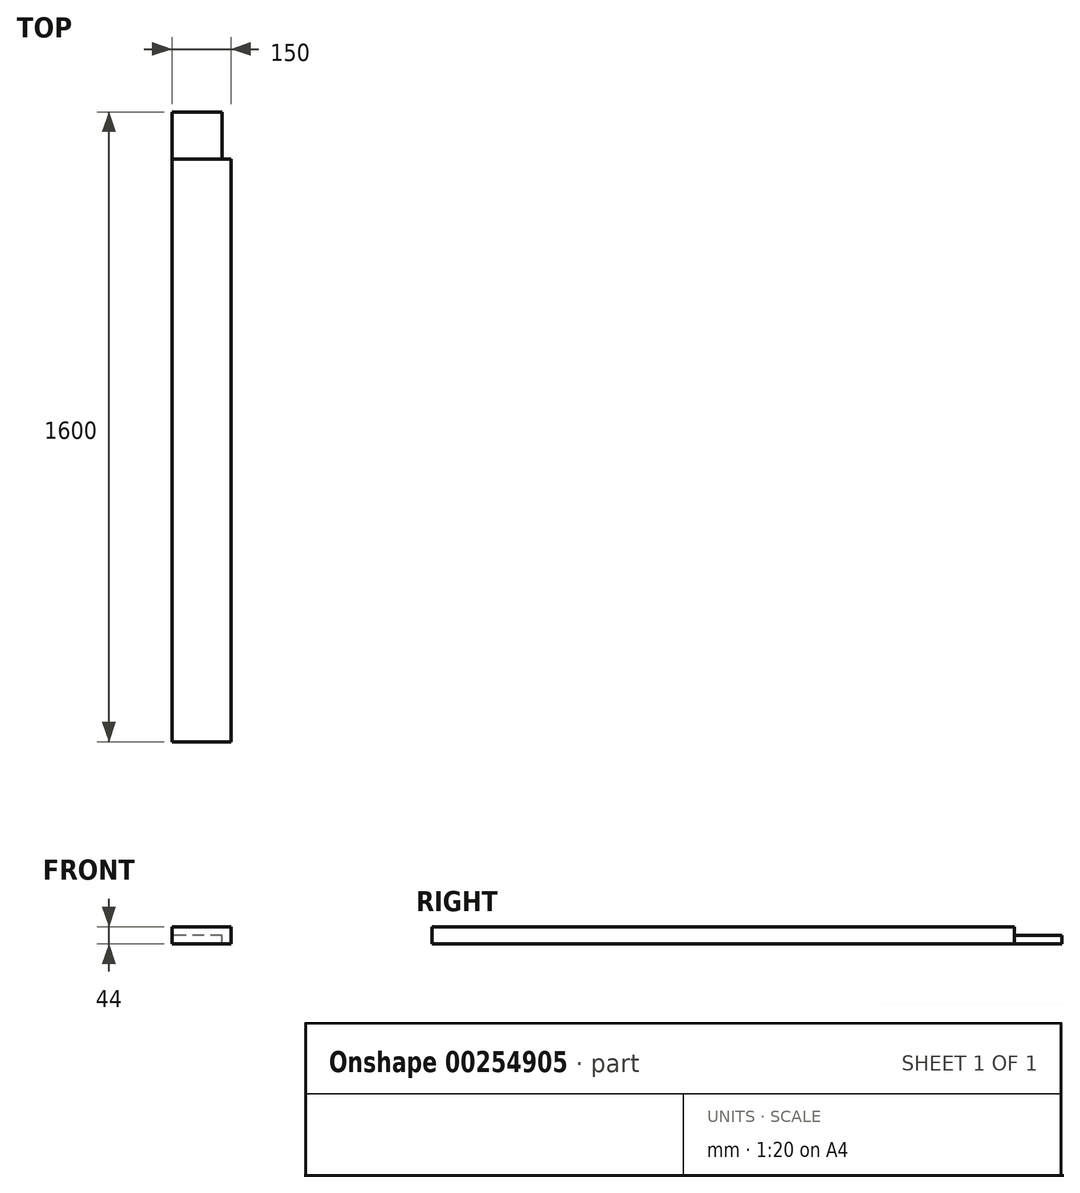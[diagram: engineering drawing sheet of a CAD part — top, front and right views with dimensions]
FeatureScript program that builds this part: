
annotation { "Feature Type Name" : "Feature", "Feature Type Description" : "" }
export const myFeature = defineFeature(function(context is Context, id is Id, definition is map)
    precondition{}
    {
        {
            var Q0;
            Q0=qCreatedBy(makeId("Front.planeOp"),FACE);
            var sketch = newSketch(context, id + "F0", { "sketchPlane" : qUnion([Q0])});
            skLineSegment(sketch, "E0.bottom", {"start": v(0, 0) * mm, "end": v(-150, 0) * mm});
            skLineSegment(sketch, "E0.top", {"start": v(0, 44) * mm, "end": v(-150, 44) * mm});
            skLineSegment(sketch, "E0.left", {"start": v(0, 0) * mm, "end": v(0, 44) * mm});
            skLineSegment(sketch, "E0.right", {"start": v(-150, 0) * mm, "end": v(-150, 44) * mm});
            skSolve(sketch);
        }
        {
            var Q0;
            Q0=makeQuery(id+"F0.imprint","IMPRINT",FACE,{"disambiguationData":[TD([[makeQuery(id+"F0.imprint","IMPRINT",EDGE,{"derivedFrom":sQuery(id+"F0.wireOp",EDGE,"E0.bottom")}),-1.0]])]});
            extrude(context, id + "F1", {"entities" : qUnion([Q0]), "oppositeDirection" : true, "depth" : 1600 * mm});
        }
        {
            var Q0;
            Q0=makeQuery(id+"F1.opExtrude","SWEPT_EDGE",EDGE,{"disambiguationData":[OSD([sQuery(id+"F0.wireOp",EDGE,"E0.bottom"),sQuery(id+"F0.wireOp",EDGE,"E0.left")])]});
            cPoint(context, id + "F2", {"entities" : qUnion([Q0]), "parameter" : 0.5});
        }
        {
            var Q0;
            Q0 = qCreatedBy(id + "F2" ,VERTEX);
            var Q1;
            Q1=qCreatedBy(makeId("Front.planeOp"),FACE);
            cPlane(context, id + "F3", {"entities" : qUnion([Q0, Q1]), "cplaneType" : CPlaneType.PLANE_POINT, "offset" : 25 * mm, "width" : 150 * mm, "height" : 150 * mm});
        }
        {
            var Q0;
            Q0=makeQuery(id+"F1.opExtrude","SWEPT_FACE",FACE,{"disambiguationData":[OSD([sQuery(id+"F0.wireOp",EDGE,"E0.top")])]});
            var sketch = newSketch(context, id + "F4", { "sketchPlane" : qUnion([Q0])});
            skLineSegment(sketch, "E1.bottom", {"start": v(0, 1600) * mm, "end": v(-22, 1600) * mm});
            skLineSegment(sketch, "E1.top", {"start": v(0, 1480) * mm, "end": v(-22, 1480) * mm});
            skLineSegment(sketch, "E1.left", {"start": v(0, 1600) * mm, "end": v(0, 1480) * mm});
            skLineSegment(sketch, "E1.right", {"start": v(-22, 1600) * mm, "end": v(-22, 1480) * mm});
            skSolve(sketch);
        }
        {
            var Q0;
            Q0=makeQuery(id+"F4.imprint","IMPRINT",FACE,{"disambiguationData":[TD([[makeQuery(id+"F4.imprint","IMPRINT",EDGE,{"derivedFrom":sQuery(id+"F4.wireOp",EDGE,"E1.bottom")}),1.0]])]});
            extrude(context, id + "F5", {"entities" : qUnion([Q0]), "operationType" : NewBodyOperationType.REMOVE, "endBound" : BoundingType.UP_TO_NEXT, "oppositeDirection" : true, "depth" : 25 * mm});
        }
        {
            var Q0;
            Q0=makeQuery(id+"F1.opExtrude","SWEPT_FACE",FACE,{"disambiguationData":[OSD([sQuery(id+"F0.wireOp",EDGE,"E0.top")])]});
            var sketch = newSketch(context, id + "F6", { "sketchPlane" : qUnion([Q0])});
            skLineSegment(sketch, "E2.bottom", {"start": v(-150, 1600) * mm, "end": v(-22, 1600) * mm});
            skLineSegment(sketch, "E2.top", {"start": v(-150, 1480) * mm, "end": v(-22, 1480) * mm});
            skLineSegment(sketch, "E2.left", {"start": v(-150, 1600) * mm, "end": v(-150, 1480) * mm});
            skLineSegment(sketch, "E2.right", {"start": v(-22, 1600) * mm, "end": v(-22, 1480) * mm});
            skSolve(sketch);
        }
        {
            var Q0;
            Q0=makeQuery(id+"F6.imprint","IMPRINT",FACE,{"disambiguationData":[TD([[makeQuery(id+"F6.imprint","IMPRINT",EDGE,{"derivedFrom":sQuery(id+"F6.wireOp",EDGE,"E2.bottom")}),1.0]])]});
            extrude(context, id + "F7", {"entities" : qUnion([Q0]), "operationType" : NewBodyOperationType.REMOVE, "oppositeDirection" : true, "depth" : 22 * mm});
        }
    });
